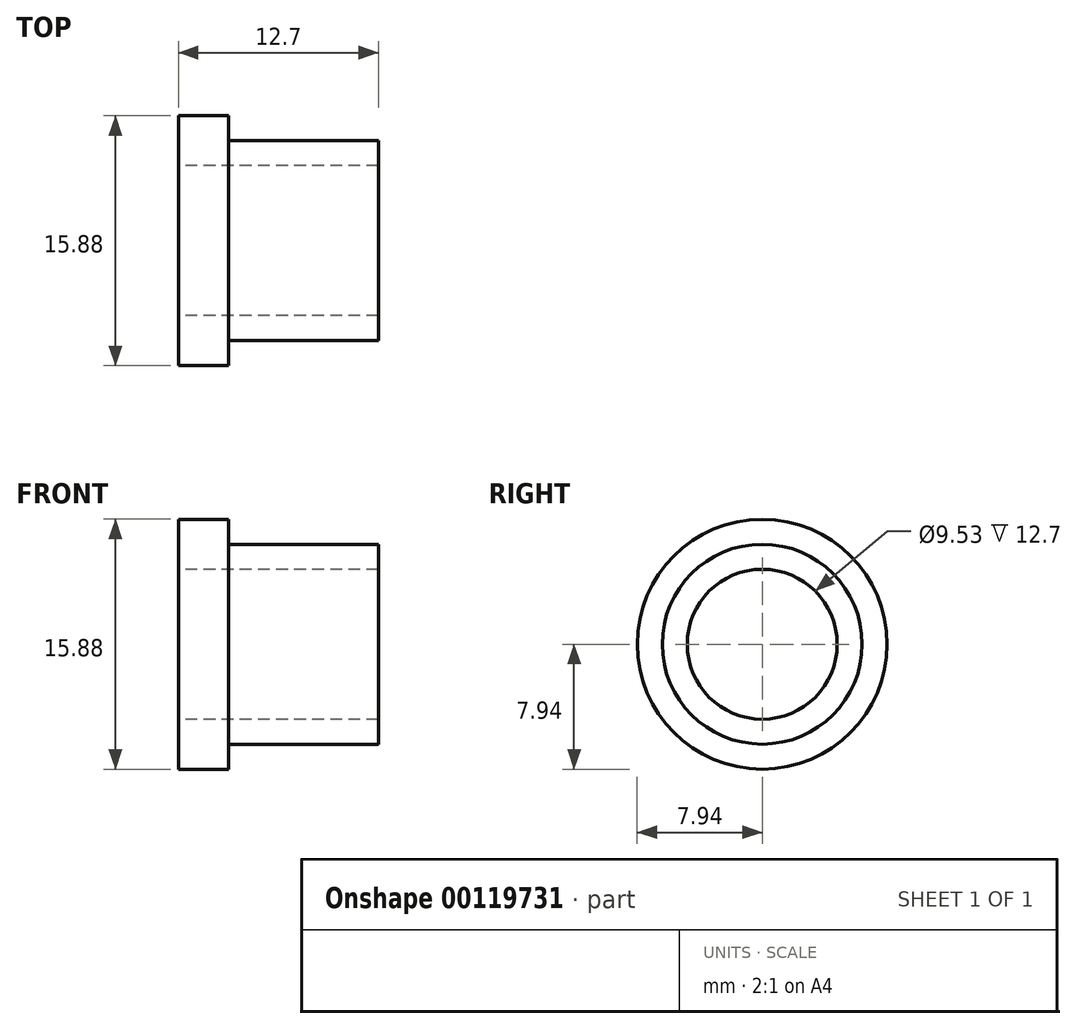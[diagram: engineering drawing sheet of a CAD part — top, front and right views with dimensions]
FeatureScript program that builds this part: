
annotation { "Feature Type Name" : "Feature", "Feature Type Description" : "" }
export const myFeature = defineFeature(function(context is Context, id is Id, definition is map)
    precondition{}
    {
        {
            var Q0;
            Q0=qCreatedBy(makeId("Front.planeOp"),FACE);
            var sketch = newSketch(context, id + "F0", { "sketchPlane" : qUnion([Q0])});
            skLineSegment(sketch, "E0", {"start": v(0, 7.94) * mm, "end": v(0, 4.76) * mm});
            skLineSegment(sketch, "E1", {"start": v(0, 4.76) * mm, "end": v(12.7, 4.76) * mm});
            skLineSegment(sketch, "E2", {"start": v(12.7, 4.76) * mm, "end": v(12.7, 6.35) * mm});
            skLineSegment(sketch, "E3", {"start": v(12.7, 6.35) * mm, "end": v(3.18, 6.35) * mm});
            skLineSegment(sketch, "E4", {"start": v(3.18, 6.35) * mm, "end": v(3.18, 7.94) * mm});
            skLineSegment(sketch, "E5", {"start": v(3.18, 7.94) * mm, "end": v(0, 7.94) * mm});
            skLineSegment(sketch, "E6", {"start": v(0, 0) * mm, "end": v(21.96, 0) * mm, "construction": true});
            skSolve(sketch);
        }
        {
            var Q0;
            Q0=qSketchRegion(id+"F0",true);
            var Q1;
            Q1=sQuery(id+"F0.wireOp",EDGE,"E6");
            revolve(context, id + "F1", {"entities" : qUnion([Q0]), "axis" : qUnion([Q1]), "revolveType" : RevolveType.FULL});
        }
    });
